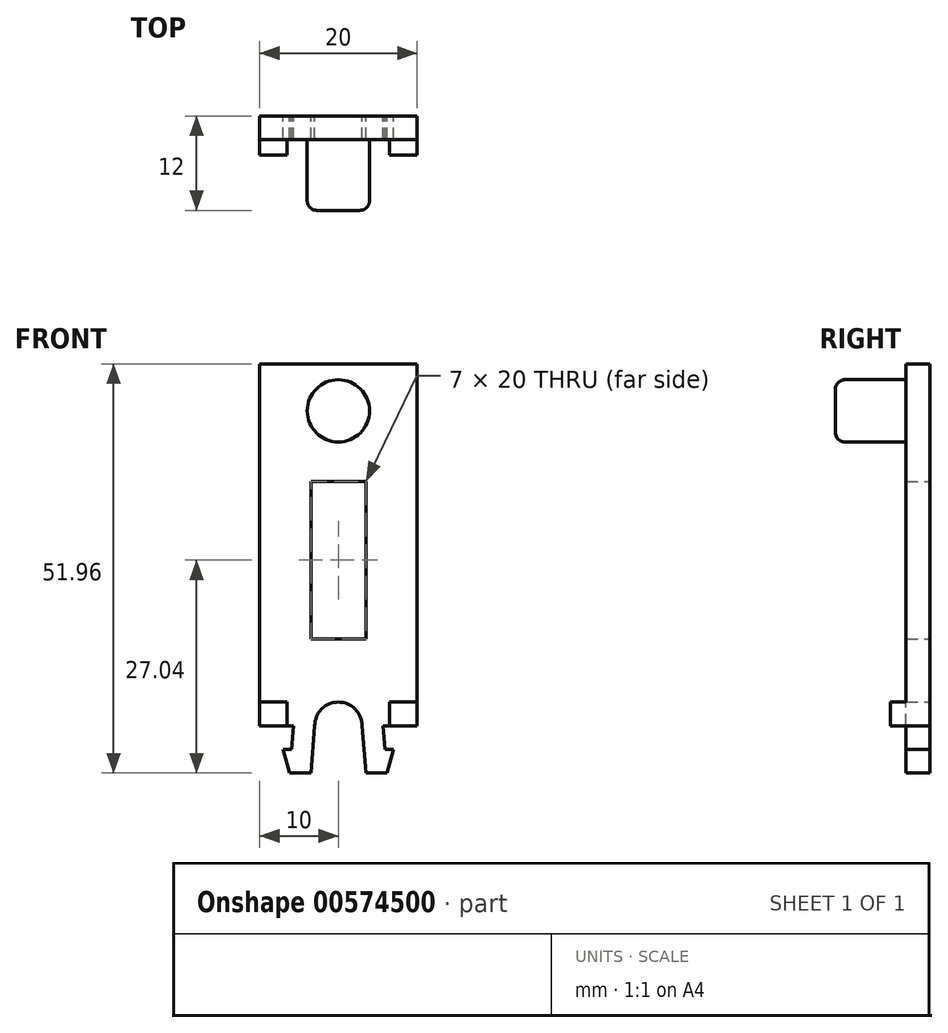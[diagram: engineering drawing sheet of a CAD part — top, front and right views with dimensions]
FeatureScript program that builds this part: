
annotation { "Feature Type Name" : "Feature", "Feature Type Description" : "" }
export const myFeature = defineFeature(function(context is Context, id is Id, definition is map)
    precondition{}
    {
        {
            var Q0;
            Q0=qCreatedBy(makeId("Front.planeOp"),FACE);
            var sketch = newSketch(context, id + "F0", { "sketchPlane" : qUnion([Q0])});
            skArc(sketch, "E0", {"start": v(3, 0) * mm, "mid": v(0, 3) * mm, "end": v(-3, 0) * mm});
            skLineSegment(sketch, "E1", {"start": v(-3, 0) * mm, "end": v(-3.5, -6) * mm});
            skLineSegment(sketch, "E2", {"start": v(-3.5, -6) * mm, "end": v(-6.2, -6) * mm});
            skLineSegment(sketch, "E3", {"start": v(-7, -3) * mm, "end": v(-5.95, -3) * mm});
            skLineSegment(sketch, "E4", {"start": v(-5.95, -3) * mm, "end": v(-5.7, 0) * mm});
            skLineSegment(sketch, "E5", {"start": v(-7, -3) * mm, "end": v(-6.2, -6) * mm});
            skLineSegment(sketch, "E6.MirrorCS", {"start": v(7, -3) * mm, "end": v(5.95, -3) * mm});
            skLineSegment(sketch, "E7.MirrorCS", {"start": v(7, -3) * mm, "end": v(6.2, -6) * mm});
            skLineSegment(sketch, "E8.MirrorCS", {"start": v(5.95, -3) * mm, "end": v(5.7, 0) * mm});
            skLineSegment(sketch, "E9.MirrorCS", {"start": v(3.5, -6) * mm, "end": v(6.2, -6) * mm});
            skLineSegment(sketch, "E10.MirrorCS", {"start": v(3, 0) * mm, "end": v(3.5, -6) * mm});
            skLineSegment(sketch, "E11.bottom", {"start": v(10, 0) * mm, "end": v(3, 0) * mm});
            skLineSegment(sketch, "E11.top", {"start": v(10, 45.96) * mm, "end": v(-10, 45.96) * mm});
            skLineSegment(sketch, "E11.left", {"start": v(10, 0) * mm, "end": v(10, 45.96) * mm});
            skLineSegment(sketch, "E11.right", {"start": v(-10, 0) * mm, "end": v(-10, 45.96) * mm});
            skPoint(sketch, "E12", {"position": v(0, 45.96) * mm});
            skCircle(sketch, "E13", {"center": v(0, 40) * mm, "radius": 3.96 * mm});
            skLineSegment(sketch, "E14.trimOffspring", {"start": v(-3, 0) * mm, "end": v(-10, 0) * mm});
            skLineSegment(sketch, "E15.bottom", {"start": v(-3.5, 31.04) * mm, "end": v(3.5, 31.04) * mm});
            skLineSegment(sketch, "E15.top", {"start": v(-3.5, 11.04) * mm, "end": v(3.5, 11.04) * mm});
            skLineSegment(sketch, "E15.left", {"start": v(-3.5, 31.04) * mm, "end": v(-3.5, 11.04) * mm});
            skLineSegment(sketch, "E15.right", {"start": v(3.5, 31.04) * mm, "end": v(3.5, 11.04) * mm});
            skPoint(sketch, "E15.middle", {"position": v(0, 21.04) * mm});
            skSolve(sketch);
        }
        {
            var Q0;
            {var subQ3=sQuery(id+"F0.wireOp",EDGE,"E0");Q0=makeQuery(id+"F0.imprint","IMPRINT",FACE,{"disambiguationData":[TD([[makeQuery(id+"F0.imprint","IMPRINT",EDGE,{"derivedFrom":subQ3}),-1.0]])]});}
            var Q1;
            {var subQ1=sQuery(id+"F0.wireOp",EDGE,"E1");Q1=makeQuery(id+"F0.imprint","IMPRINT",FACE,{"disambiguationData":[TD([[makeQuery(id+"F0.imprint","IMPRINT",EDGE,{"derivedFrom":subQ1}),-1.0]])]});}
            var Q2;
            Q2=makeQuery(id+"F0.imprint","IMPRINT",FACE,{"disambiguationData":[TD([[makeQuery(id+"F0.imprint","IMPRINT",EDGE,{"derivedFrom":sQuery(id+"F0.wireOp",EDGE,"E6.MirrorCS")}),1.0]])]});
            extrude(context, id + "F1", {"entities" : qUnion([Q0, Q1, Q2]), "depth" : 3 * mm, "offsetDistance" : 25 * mm});
        }
        {
            var Q0;
            Q0=makeQuery(id+"F1.opExtrude","CAP_FACE",FACE,{"disambiguationData":[OSD([sQuery(id+"F0.wireOp",EDGE,"E0"),sQuery(id+"F0.wireOp",EDGE,"E1"),sQuery(id+"F0.wireOp",EDGE,"E2"),sQuery(id+"F0.wireOp",EDGE,"E3"),sQuery(id+"F0.wireOp",EDGE,"E4"),sQuery(id+"F0.wireOp",EDGE,"E5"),sQuery(id+"F0.wireOp",EDGE,"E6.MirrorCS"),sQuery(id+"F0.wireOp",EDGE,"E7.MirrorCS"),sQuery(id+"F0.wireOp",EDGE,"E8.MirrorCS"),sQuery(id+"F0.wireOp",EDGE,"E9.MirrorCS"),sQuery(id+"F0.wireOp",EDGE,"E10.MirrorCS"),sQuery(id+"F0.wireOp",EDGE,"E11.bottom"),sQuery(id+"F0.wireOp",EDGE,"E11.top"),sQuery(id+"F0.wireOp",EDGE,"E11.left"),sQuery(id+"F0.wireOp",EDGE,"E11.right"),sQuery(id+"F0.wireOp",EDGE,"E13"),sQuery(id+"F0.wireOp",EDGE,"E14.trimOffspring"),sQuery(id+"F0.wireOp",EDGE,"E15.bottom"),sQuery(id+"F0.wireOp",EDGE,"E15.top"),sQuery(id+"F0.wireOp",EDGE,"E15.left"),sQuery(id+"F0.wireOp",EDGE,"E15.right")])],"isStart":true});
            var sketch = newSketch(context, id + "F2", { "sketchPlane" : qUnion([Q0])});
            skCircle(sketch, "E16.0", {"center": v(0, 40) * mm, "radius": 3.96 * mm});
            skSolve(sketch);
        }
        {
            var Q0;
            Q0=makeQuery(id+"F2.imprint","IMPRINT",FACE,{"disambiguationData":[TD([[makeQuery(id+"F2.imprint","IMPRINT",EDGE,{"derivedFrom":sQuery(id+"F2.wireOp",EDGE,"E16.0")}),-1.0]])]});
            extrude(context, id + "F3", {"entities" : qUnion([Q0]), "operationType" : NewBodyOperationType.ADD, "oppositeDirection" : true, "depth" : (9 + 3) * mm, "offsetDistance" : 25 * mm});
        }
        {
            var Q0;
            Q0=makeQuery(id+"F3.opExtrude","CAP_EDGE",EDGE,{"disambiguationData":[OSD([sQuery(id+"F2.wireOp",EDGE,"E16.0")])],"isStart":false});
            fillet(context, id + "F4", {"entities" : qUnion([Q0]), "radius" : 1.25 * mm, "tangentPropagation" : true, "allowEdgeOverflow" : false});
        }
        {
            var Q0;
            Q0=makeQuery(id+"F1.opExtrude","CAP_FACE",FACE,{"disambiguationData":[OSD([sQuery(id+"F0.wireOp",EDGE,"E0"),sQuery(id+"F0.wireOp",EDGE,"E1"),sQuery(id+"F0.wireOp",EDGE,"E2"),sQuery(id+"F0.wireOp",EDGE,"E3"),sQuery(id+"F0.wireOp",EDGE,"E4"),sQuery(id+"F0.wireOp",EDGE,"E5"),sQuery(id+"F0.wireOp",EDGE,"E6.MirrorCS"),sQuery(id+"F0.wireOp",EDGE,"E7.MirrorCS"),sQuery(id+"F0.wireOp",EDGE,"E8.MirrorCS"),sQuery(id+"F0.wireOp",EDGE,"E9.MirrorCS"),sQuery(id+"F0.wireOp",EDGE,"E10.MirrorCS"),sQuery(id+"F0.wireOp",EDGE,"E11.bottom"),sQuery(id+"F0.wireOp",EDGE,"E11.top"),sQuery(id+"F0.wireOp",EDGE,"E11.left"),sQuery(id+"F0.wireOp",EDGE,"E11.right"),sQuery(id+"F0.wireOp",EDGE,"E13"),sQuery(id+"F0.wireOp",EDGE,"E14.trimOffspring"),sQuery(id+"F0.wireOp",EDGE,"E15.bottom"),sQuery(id+"F0.wireOp",EDGE,"E15.top"),sQuery(id+"F0.wireOp",EDGE,"E15.left"),sQuery(id+"F0.wireOp",EDGE,"E15.right")])],"isStart":false});
            var sketch = newSketch(context, id + "F5", { "sketchPlane" : qUnion([Q0])});
            skLineSegment(sketch, "E17.bottom", {"start": v(-10, 0) * mm, "end": v(-6.5, 0) * mm});
            skLineSegment(sketch, "E17.top", {"start": v(-10, 3) * mm, "end": v(-6.5, 3) * mm});
            skLineSegment(sketch, "E17.left", {"start": v(-10, 0) * mm, "end": v(-10, 3) * mm});
            skLineSegment(sketch, "E17.right", {"start": v(-6.5, 0) * mm, "end": v(-6.5, 3) * mm});
            skLineSegment(sketch, "E18.MirrorCS", {"start": v(10, 0) * mm, "end": v(6.5, 0) * mm});
            skLineSegment(sketch, "E19.MirrorCS", {"start": v(6.5, 0) * mm, "end": v(6.5, 3) * mm});
            skLineSegment(sketch, "E20.MirrorCS", {"start": v(10, 0) * mm, "end": v(10, 3) * mm});
            skLineSegment(sketch, "E21.MirrorCS", {"start": v(10, 3) * mm, "end": v(6.5, 3) * mm});
            skSolve(sketch);
        }
        {
            var Q0;
            Q0=makeQuery(id+"F5.imprint","IMPRINT",FACE,{"disambiguationData":[TD([[makeQuery(id+"F5.imprint","IMPRINT",EDGE,{"derivedFrom":sQuery(id+"F5.wireOp",EDGE,"E17.bottom")}),-1.0]])]});
            var Q1;
            Q1=makeQuery(id+"F5.imprint","IMPRINT",FACE,{"disambiguationData":[TD([[makeQuery(id+"F5.imprint","IMPRINT",EDGE,{"derivedFrom":sQuery(id+"F5.wireOp",EDGE,"E18.MirrorCS")}),-1.0]])]});
            extrude(context, id + "F6", {"entities" : qUnion([Q0, Q1]), "operationType" : NewBodyOperationType.ADD, "depth" : 2 * mm, "offsetDistance" : 25 * mm});
        }
    });
